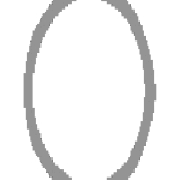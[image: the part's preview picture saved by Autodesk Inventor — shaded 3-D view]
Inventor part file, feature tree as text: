
AUTODESK INVENTOR PART (.ipt)
format: ipt  version: 2021 (Build 250183000, 183)  size: 109,568 bytes
history: native  units: in
note: dims shown in document units (in); Inventor stores cm internally (conversion verified against a paired STEP export)
features: other x4, sketch x3, plane x1
ambient origin geometry x8: Origin, YZ Plane, XZ Plane, XY Plane, X Axis, Y Axis, Z Axis, Center Point
bodies: Solid1 (feature_tree), Body (feature_tree)
feature tree (8):
  other  "Driven Length"
  other  "Frame Generator"
  other  "Start Plane"
  other  "End Plane"
  sketch  "Sketch"  dims[d2=15.2522in d4=-0.0in d5=15.2522in d6=0.12in d7=0.0in d8=90.0deg d9=15.2522in]
  sketch  "Sketch2"  dims[d0=1.0in]
  plane  "Work Plane3"
  sketch  "Sketch3"  dims[d1=0.065in]
